# Revit family: PD4-C-AP types Avec hôte
name_source: partatom
category: Dispositifs d'éclairage
units: mm (PartAtom-declared; Revit-internal decimal feet)

## family parameters
Conserver l'orientation des annotations = Oui
Cote de connecteur circulaire = Utiliser le diamètre
Couper avec des vides une fois chargée = Non
Hôte = Face
Partagée = Non
Point de calcul de pièce = Non
Type d'élément = Normal

## types (15) — shared parameters
Classe = II
Code d'assemblage = D5010200
Fabricant = B.E.G.
Hauteur de montage max = 280 cm
Image du type = COULOIR.jpg
Marque = LUXOMAT
Mode de pose = Saillie
Température ambiante = -25°C à +50°C
URL = http://www.luxomat.com
zero-valued in all types: Elévation par défaut

## per-type parameters (varying)
| type | Alimentation | Charge Cos ɸ =0.5 | Charge Cos ɸ =1 | Charge LED | Commentaires du type | Consommation | IP | Modèle | Relais | Référence | Type de Sortie |
| 01- PD4-C-AP Générique | 110-240 V AC |  |  |  | DET.PRES.SPECIAL COULOIR.180/360°/2x10M APPARENT |  | 44 ou 54 | PD4-C-AP |  |  |  |
| 02- PD4N-1C-C-AP réf 92270 | 110-240 V AC | 1150 VA | 2300 W | 300 W | DET.MOUV.SPECIAL COULOIR.1 CONTACT.180/360°/2x10M APPARENT | 0,25 W | 44 | PD4N-1C-C-AP | 10 A | 92270 | TOR |
| 03- PD4-M-1C-C-AP réf 92587 | 110-240 V AC | 1150 VA | 2300 W | 300 W | DET.PRES.SPECIAL COULOIR.MAITRE.1 CONTACT.180/360°/2x10M APPARENT | 0,45 W | 54 | PD4-M-1C-C-AP | 10 A | 92587 | TOR |
| 04- PD4-M-1C-C-SP-AP réf 92485 | 110-240 V AC | 1150 VA | 2300 W | 300 W | DET.PRES.SPECIAL COULOIR.MAITRE.1 CONTACT.SECURITE POSITIVE.180/360°/2x10M APPARENT | 0,45 W | 54 | PD4-M-1C-C-SP-AP | 10 A | 92485 | TOR / Sécurité Positive |
| 05- PD4-M-2C-C-AP réf 92440 | 110-240 V AC | 1150 VA | 2300 W | 300 W | DET.PRES.SPECIAL COULOIR.MAITRE.2 CONTACTS.180/360°/2x10M APPARENT | 0,47 W | 54 | PD4-M-2C-C-AP | 10 A / 3 A | 92440 | TOR + CVC |
| 08- PD4-M-DIM-C-AP réf 92218 | 110-240 V AC | 1150 VA | 2300 W | 300 W | DET.PRES.SPECIAL COULOIR.MAITRE.DIM(1-10V).180/360°/2x10M APPARENT | 0,50 W | 54 | PD4-M-DIM-C-AP | 10 A | 92218 | DIM (50 ballasts maxi) |
| 06- PD4N-M-DACO-C-AP réf 93460 | 110-240 V AC | 0 | 0 | 0 | DET.PRES.SPECIAL COULOIR.MAITRE.DALI 2.180/360°/2x10M APPARENT + KIT AP réf 93465 + Lentille Couloir réf 93073 | 2 W | 54 | PD4N-M-DACO-C-AP | 0 | 93460+93465+93073 | DALI 2  (40 drivers maxi) |
| 13- PD4N-KNX-C-DX-AP réf 93389 | 24 V DC par Bus KNX | 0 | 0 | 0 | DET.PRES.SPECIAL COULOIR.KNX.VERSION DELUXE.180/360°/2x10M ENCASTRE + KIT AP réf 93307 | 12 mA | 54 | PD4N-KNX-C-DX-AP | 0 | 93389+93307 | KNX - 1 sortie Eclairage TOR ou GRADATION / 3 sorties Présence / Capteur de température et bruit |
| 09- PD4-S-C-AP réf 92442 | 110-240 V AC | 0 | 0 | 0 | DET.PRES.SPECIAL COULOIR.ESCLAVE.180/360°/2x10M APPARENT | 0,25 W | 54 | PD4-S-C-AP | 0 | 92442 | Esclave |
| 12- PD4N-BMS-DALI-2-C-AP réf 93546 | 10-22 V DC par Bus DALI | 0 | 0 | 0 | MULTI.CAPTEUR.PRES.SPECIAL COULOIR.BMS.DALI2.180/360°/2x10M APPARENT + KIT AP réf 93307 + Lentille Couloir réf 93073 | 7 mA | 54 | PD4N-BMS-DALI-2-C-AP | 0 | 93546 | DALI 2 adressable - BMS |
| 11- PD4N-DALISYS-C-AP réf 93340 | 10-22 V DC par Bus DALI | 0 | 0 | 0 | MULTI.CAPTEUR.PRES.SPECIAL COULOIR.DALISYS.180/360°/2x10M ENCASTRE + KIT AP réf 93307 + Lentille Couloir réf 93073 | 7 mA | 54 | PD4N-DALISYS-C-AP | 0 | 93340+93307+93073 | DALI adressable |
| 10- PD4N-DALILINK-C-AP réf 93377 | 16 V DC par Bus DALI | 0 | 0 | 0 | MULTI.CAPTEUR.PRES.SPECIAL COULOIR.DALILINK.180/360°/2x10M ENCASTRE + KIT AP réf 93307 + Lentille Couloir réf 93073 | 7 mA | 54 | PD4N-DALILINK-C-AP | 0 | 93377+93307+93073 | DALILINK |
| 14- PD4N-KNXs-C-ST-AP réf 93515 | 24 V DC par Bus KNX | 0 | 0 | 0 | DET.PRES.SPECIAL COULOIR.KNX Sécure.VERSION STANDARD.180/360°/2x10M ENCASTRE + KIT AP réf 93307 + Lentille Couloir réf 93073 | 12 mA | 54 | PD4N-KNXs-C-ST-AP | 0 | 93515+93307+93073 | KNX Sécure - 1 sortie Eclairage TOR ou GRADATION / 3 sorties Présence / HCL |
| 15- PD4N-KNXs-C-DX-AP réf 93517 | 24 V DC par Bus KNX | 0 | 0 | 0 | DET.PRES.SPECIAL COULOIR.KNX Sécure.VERSION DELUXE.180/360°/2x10M ENCASTRE + KIT AP réf 93307 + Lentille Couloir réf 93073 | 12 mA | 54 | PD4N-KNXs-C-DX-AP | 0 | 93517+93307+93073 | KNX Sécure - 1 sortie Eclairage TOR ou GRADATION / 3 sorties Présence / Capteur de température et bruit / HCL |
| 07- PD4N-M-DACO-1C-C-AP réf 93463 | 110-240 V AC | 1150 VA | 2300 W | 300 W | DET.PRES.SPECIAL COULOIR.MAITRE.DALI 2 + CONTACT NO.180/360°/2x10M APPARENT + KIT AP réf 93465 + Lentille Couloir réf 93073 | 2 W | 54 | PD4N-M-DACO-1C-C-AP | 10 A | 93463+93465+93073 | DALI 2 (40 drivers maxi) + Contact NO |

## geometry (parser evidence)
native form markers: Blend x10
no freeform markers — native parametric forms only
